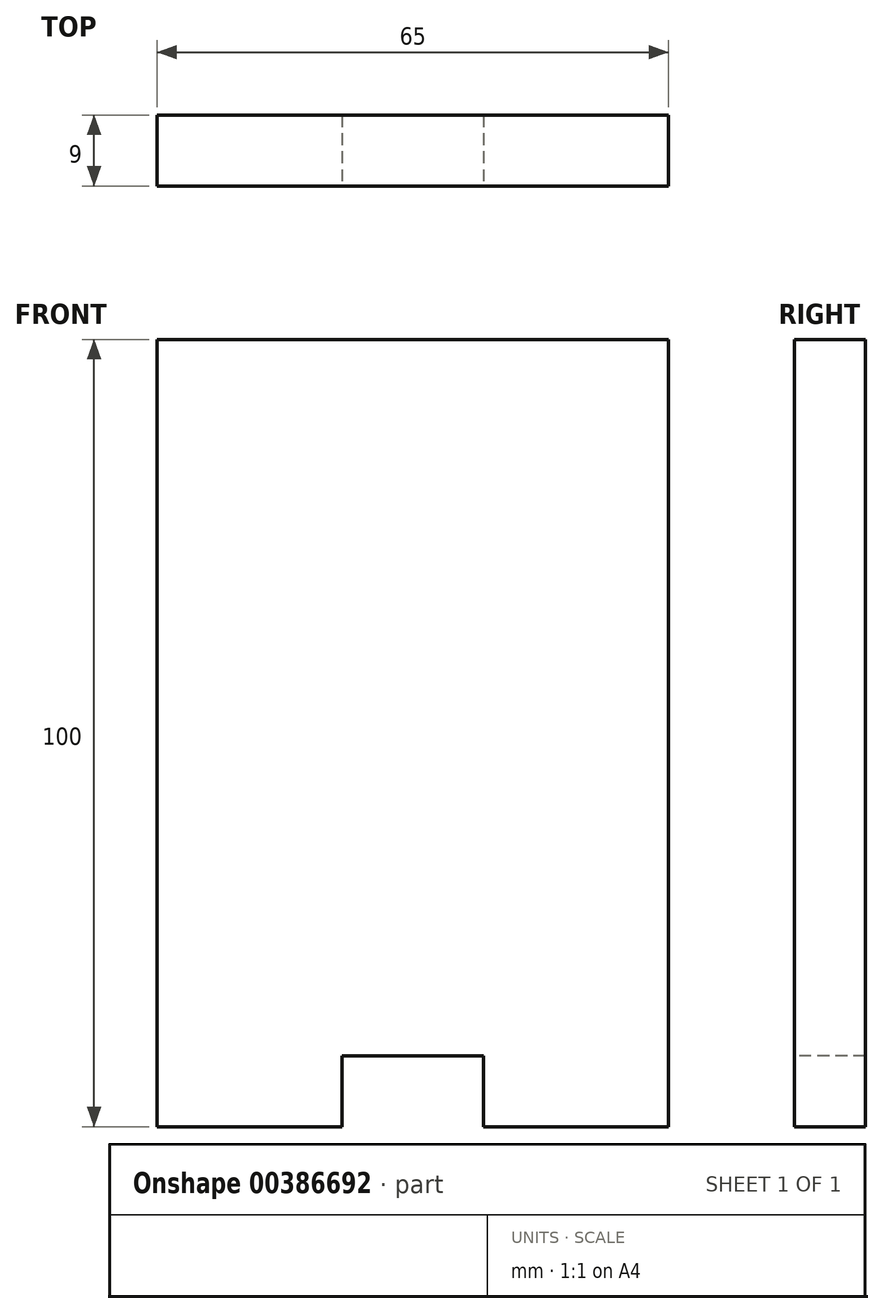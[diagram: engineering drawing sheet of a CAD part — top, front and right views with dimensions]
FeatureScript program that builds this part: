
annotation { "Feature Type Name" : "Feature", "Feature Type Description" : "" }
export const myFeature = defineFeature(function(context is Context, id is Id, definition is map)
    precondition{}
    {
        {
            var Q0;
            Q0=qCreatedBy(makeId("Front.planeOp"),FACE);
            var sketch = newSketch(context, id + "F0", { "sketchPlane" : qUnion([Q0])});
            skLineSegment(sketch, "E0.bottom", {"start": v(-32.5, 50) * mm, "end": v(32.5, 50) * mm});
            skLineSegment(sketch, "E0.top", {"start": v(-32.5, -50) * mm, "end": v(32.5, -50) * mm});
            skLineSegment(sketch, "E0.left", {"start": v(-32.5, 50) * mm, "end": v(-32.5, -50) * mm});
            skLineSegment(sketch, "E0.right", {"start": v(32.5, 50) * mm, "end": v(32.5, -50) * mm});
            skPoint(sketch, "E0.middle", {"position": v(0, 0) * mm});
            skSolve(sketch);
        }
        {
            var Q0;
            Q0 = qSketchRegion(id + "F0", true);
            extrude(context, id + "F1", {"entities" : qUnion([Q0]), "depth" : 9 * mm});
        }
        {
            var Q0;
            Q0=makeQuery(id+"F1.opExtrude","CAP_FACE",FACE,{"disambiguationData":[OSD([sQuery(id+"F0.wireOp",EDGE,"E0.bottom"),sQuery(id+"F0.wireOp",EDGE,"E0.top"),sQuery(id+"F0.wireOp",EDGE,"E0.left"),sQuery(id+"F0.wireOp",EDGE,"E0.right")])],"isStart":false});
            var sketch = newSketch(context, id + "F2", { "sketchPlane" : qUnion([Q0])});
            skLineSegment(sketch, "E1", {"start": v(0, -50) * mm, "end": v(0, -41) * mm, "construction": true});
            skPoint(sketch, "E1.endSnap0", {"position": v(0, -50) * mm});
            skLineSegment(sketch, "E2", {"start": v(0, -41) * mm, "end": v(9, -41) * mm});
            skLineSegment(sketch, "E3", {"start": v(9, -41) * mm, "end": v(9, -50) * mm});
            skLineSegment(sketch, "E4", {"start": v(9, -50) * mm, "end": v(0, -50) * mm});
            skLineSegment(sketch, "E5.MirrorCS", {"start": v(0, -41) * mm, "end": v(-9, -41) * mm});
            skLineSegment(sketch, "E6.MirrorCS", {"start": v(-9, -41) * mm, "end": v(-9, -50) * mm});
            skLineSegment(sketch, "E7.MirrorCS", {"start": v(-9, -50) * mm, "end": v(0, -50) * mm});
            skSolve(sketch);
        }
        {
            var Q0;
            Q0=makeQuery(id+"F2.imprint","IMPRINT",FACE,{"disambiguationData":[TD([[makeQuery(id+"F2.imprint","IMPRINT",EDGE,{"derivedFrom":sQuery(id+"F2.wireOp",EDGE,"E2")}),-1.0]])]});
            extrude(context, id + "F3", {"entities" : qUnion([Q0]), "operationType" : NewBodyOperationType.REMOVE, "endBound" : BoundingType.THROUGH_ALL, "oppositeDirection" : true, "depth" : 25 * mm});
        }
    });
